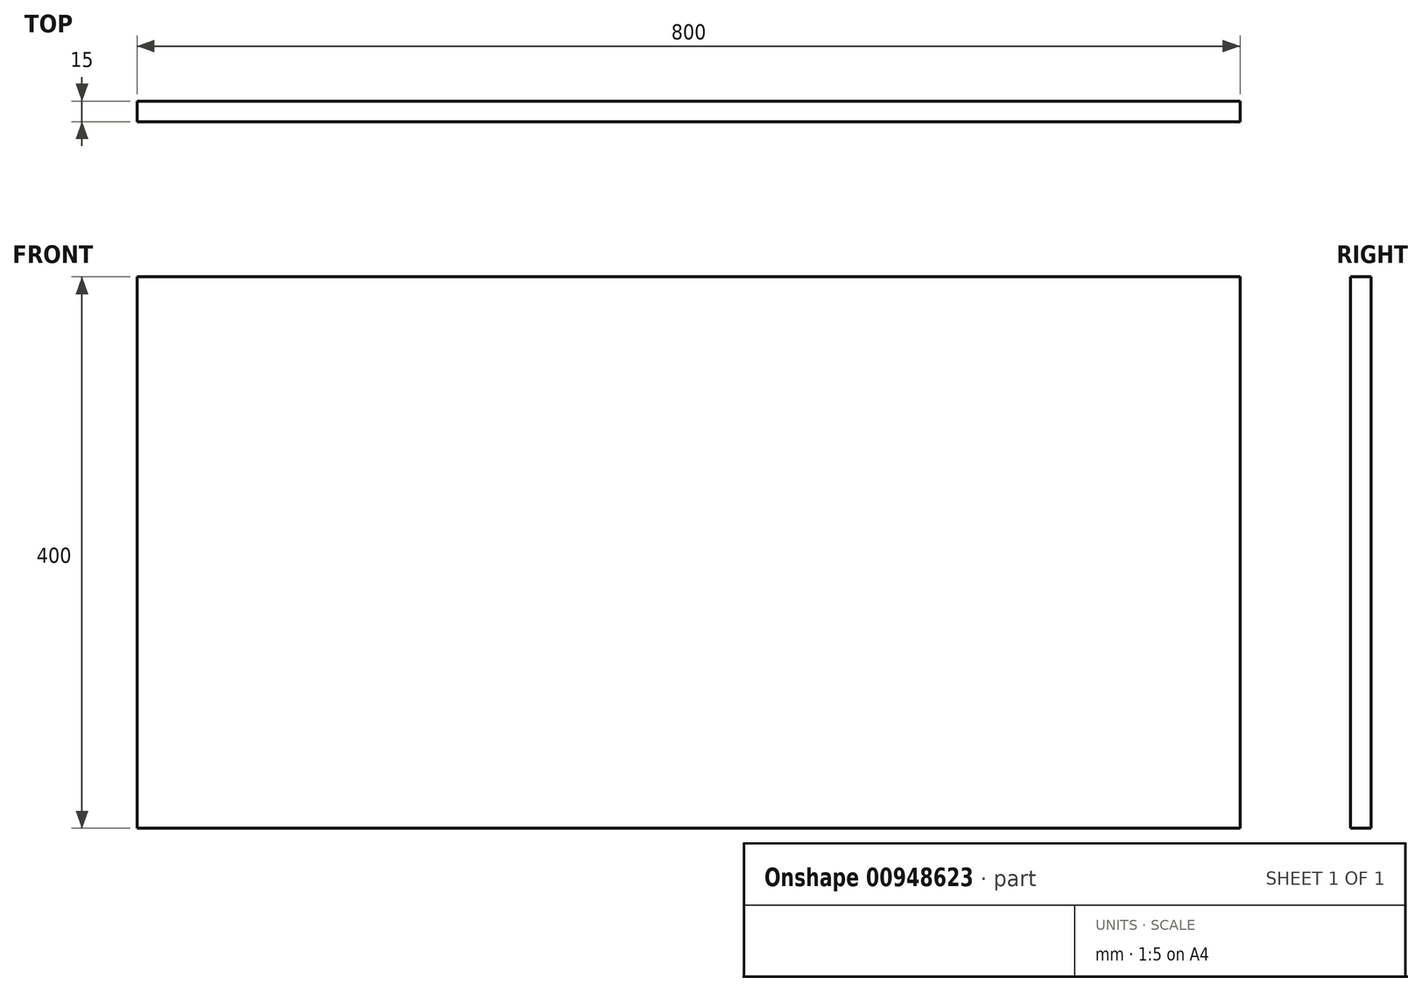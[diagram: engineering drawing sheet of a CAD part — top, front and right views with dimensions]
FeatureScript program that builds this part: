
annotation { "Feature Type Name" : "Feature", "Feature Type Description" : "" }
export const myFeature = defineFeature(function(context is Context, id is Id, definition is map)
    precondition{}
    {
        {
            var Q0;
            Q0=qCreatedBy(makeId("Front.planeOp"),FACE);
            var sketch = newSketch(context, id + "F0", { "sketchPlane" : qUnion([Q0])});
            skLineSegment(sketch, "E0.bottom", {"start": v(0, 0) * mm, "end": v(800, 0) * mm});
            skLineSegment(sketch, "E0.top", {"start": v(0, 400) * mm, "end": v(800, 400) * mm});
            skLineSegment(sketch, "E0.left", {"start": v(0, 0) * mm, "end": v(0, 400) * mm});
            skLineSegment(sketch, "E0.right", {"start": v(800, 0) * mm, "end": v(800, 400) * mm});
            skSolve(sketch);
        }
        {
            var Q0;
            Q0 = qSketchRegion(id + "F0", true);
            extrude(context, id + "F1", {"entities" : qUnion([Q0]), "depth" : 15 * mm, "offsetDistance" : 25 * mm});
        }
    });
